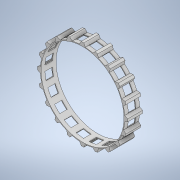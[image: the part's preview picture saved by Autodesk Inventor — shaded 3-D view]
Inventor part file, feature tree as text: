
AUTODESK INVENTOR PART (.ipt)
format: ipt  version: 2020 (Build 240168000, 168)  size: 444,416 bytes
history: native  units: mm
features: extrude x4, other x2, chamfer x2, sketch x2, pattern_circular x1
ambient origin geometry x8: Origin, YZ Plane, XZ Plane, XY Plane, X Axis, Y Axis, Z Axis, Center Point
bodies: Body1 (feature_tree)
feature tree (11):
  other  "Bryła1"
  extrude  "Wyciągnięcie proste1"  Depth=111.109mm
  other  "Płaszczyzna konstrukcyjna1"
  extrude  "Wyciągnięcie proste2"  Depth=1.0mm
  chamfer  "Faza1"  Distance=20.0mm
  chamfer  "Faza2"  Distance=7.528mm
  pattern_circular  "Szyk kołowy1"  [2 undecoded]
  extrude  "Wyciągnięcie proste3"  Depth=2.0mm TaperAngle=45.0deg
  extrude  "Wyciągnięcie proste4"  Depth=2.0mm TaperAngle=45.0deg
  sketch  "Szkic1"
  sketch  "Szkic2"
note: 2 required parameter values undecoded (feature->parameter linkage not recoverable at this tier; creation-order binding heuristic only, values carry confidence <= 0.55)
